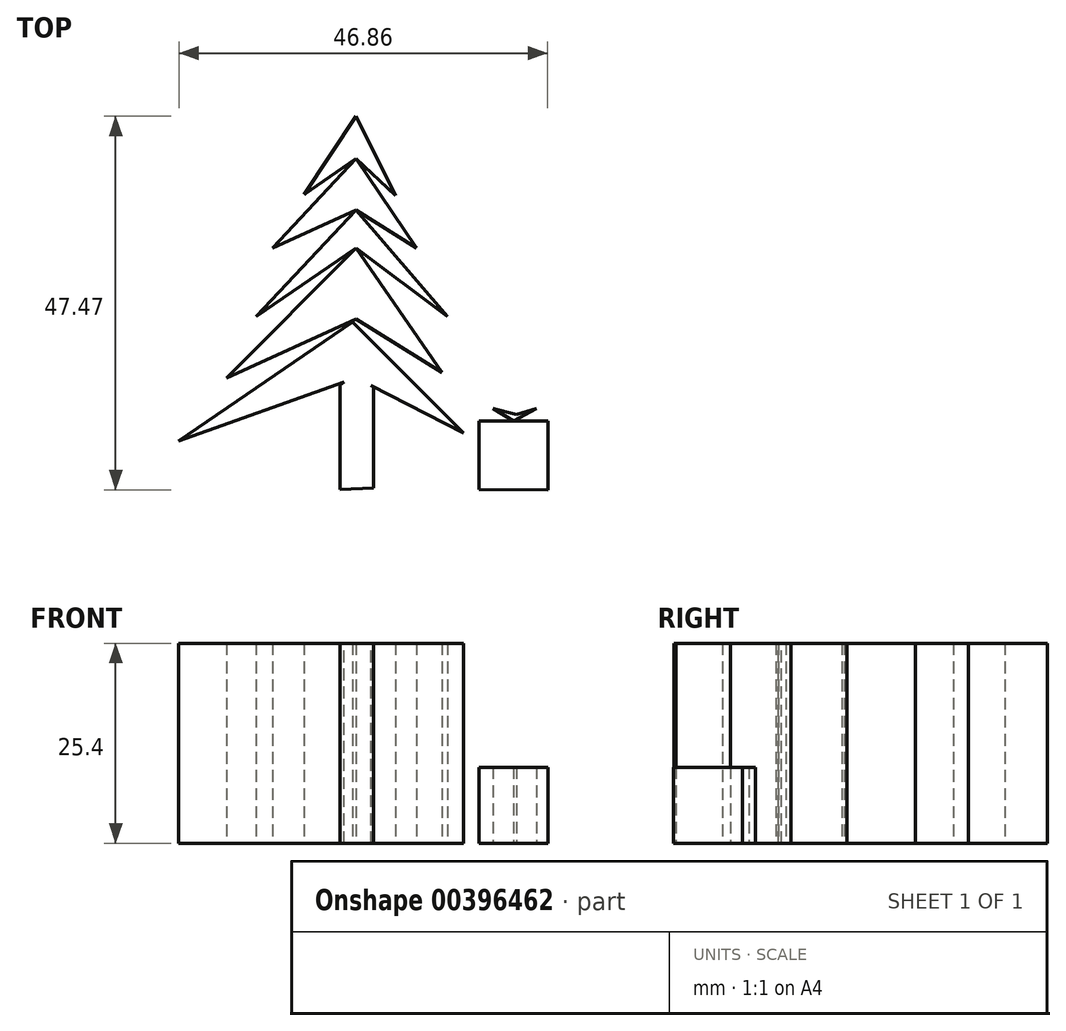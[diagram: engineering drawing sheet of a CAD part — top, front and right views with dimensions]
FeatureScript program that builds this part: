
annotation { "Feature Type Name" : "Feature", "Feature Type Description" : "" }
export const myFeature = defineFeature(function(context is Context, id is Id, definition is map)
    precondition{}
    {
        {
            var Q0;
            Q0=qCreatedBy(makeId("Top.planeOp"),FACE);
            var sketch = newSketch(context, id + "F0", { "sketchPlane" : qUnion([Q0])});
            skLineSegment(sketch, "E0", {"start": v(-12.69, -29.61) * mm, "end": v(0, -20.88) * mm});
            skLineSegment(sketch, "E1", {"start": v(0, -20.88) * mm, "end": v(11.61, -29.58) * mm});
            skLineSegment(sketch, "E2", {"start": v(-12.69, -29.61) * mm, "end": v(0, -16.07) * mm});
            skLineSegment(sketch, "E3", {"start": v(0, -16.07) * mm, "end": v(-10.65, -20.88) * mm});
            skLineSegment(sketch, "E4", {"start": v(-10.65, -20.88) * mm, "end": v(0, -9.51) * mm});
            skLineSegment(sketch, "E5", {"start": v(0, -9.51) * mm, "end": v(-6.63, -14.07) * mm});
            skLineSegment(sketch, "E6", {"start": v(-6.63, -14.07) * mm, "end": v(0, -4.13) * mm});
            skLineSegment(sketch, "E7", {"start": v(0, -16.07) * mm, "end": v(11.61, -29.58) * mm});
            skLineSegment(sketch, "E8", {"start": v(0, -16.07) * mm, "end": v(7.66, -20.88) * mm});
            skLineSegment(sketch, "E9", {"start": v(0, -9.51) * mm, "end": v(7.66, -20.88) * mm});
            skLineSegment(sketch, "E10", {"start": v(0, -9.51) * mm, "end": v(5, -14.2) * mm});
            skLineSegment(sketch, "E11", {"start": v(0, -4.13) * mm, "end": v(5, -14.2) * mm});
            skLineSegment(sketch, "E12", {"start": v(0, -20.88) * mm, "end": v(-16.49, -37.36) * mm});
            skLineSegment(sketch, "E13", {"start": v(0, -20.88) * mm, "end": v(10.9, -36.72) * mm});
            skLineSegment(sketch, "E14", {"start": v(-16.49, -37.36) * mm, "end": v(0, -29.91) * mm});
            skLineSegment(sketch, "E15", {"start": v(0, -29.91) * mm, "end": v(10.9, -36.72) * mm});
            skLineSegment(sketch, "E16", {"start": v(0, -29.91) * mm, "end": v(-22.53, -45.41) * mm});
            skLineSegment(sketch, "E17", {"start": v(-0.5, -30.24) * mm, "end": v(13.63, -44.38) * mm});
            skLineSegment(sketch, "E18", {"start": v(-22.53, -45.41) * mm, "end": v(0, -37.36) * mm});
            skLineSegment(sketch, "E19", {"start": v(0, -37.36) * mm, "end": v(13.63, -44.38) * mm});
            skLineSegment(sketch, "E20", {"start": v(0, 8.52) * mm, "end": v(-3.74, 0) * mm});
            skLineSegment(sketch, "E21", {"start": v(0, 8.52) * mm, "end": v(3.8, 0) * mm});
            skLineSegment(sketch, "E22", {"start": v(3.8, 0) * mm, "end": v(10.42, 2.95) * mm});
            skLineSegment(sketch, "E23", {"start": v(10.42, 2.95) * mm, "end": v(3.8, -2.33) * mm});
            skLineSegment(sketch, "E24", {"start": v(3.8, -2.33) * mm, "end": v(7.15, -6.53) * mm});
            skLineSegment(sketch, "E25", {"start": v(7.15, -6.53) * mm, "end": v(0, -4.13) * mm});
            skLineSegment(sketch, "E26", {"start": v(-3.74, 0) * mm, "end": v(-10.47, 2.95) * mm});
            skLineSegment(sketch, "E27", {"start": v(-10.47, 2.95) * mm, "end": v(-6.24, -2.33) * mm});
            skLineSegment(sketch, "E28", {"start": v(-6.24, -2.33) * mm, "end": v(-8.09, -6.53) * mm});
            skLineSegment(sketch, "E29", {"start": v(-7.4, -6.56) * mm, "end": v(0, -4.13) * mm});
            skSolve(sketch);
        }
        {
            var Q0;
            Q0 = qSketchRegion(id + "F0", true);
            extrude(context, id + "F1", {"entities" : qUnion([Q0]), "depth" : 25.4 * mm});
        }
        {
            var Q0;
            Q0=qCreatedBy(makeId("Top.planeOp"),FACE);
            var sketch = newSketch(context, id + "F2", { "sketchPlane" : qUnion([Q0])});
            skLineSegment(sketch, "E30", {"start": v(2.19, -38.6) * mm, "end": v(2.19, -51.33) * mm});
            skLineSegment(sketch, "E31", {"start": v(-2.06, -38.3) * mm, "end": v(-2.06, -51.55) * mm});
            skLineSegment(sketch, "E32", {"start": v(2.19, -51.33) * mm, "end": v(-2.06, -51.55) * mm});
            skLineSegment(sketch, "E33", {"start": v(2.19, -38.6) * mm, "end": v(0, -36.75) * mm});
            skLineSegment(sketch, "E34", {"start": v(-2.06, -38.3) * mm, "end": v(0, -36.75) * mm});
            skSolve(sketch);
        }
        {
            var Q0;
            Q0 = qSketchRegion(id + "F2", true);
            extrude(context, id + "F3", {"entities" : qUnion([Q0]), "operationType" : NewBodyOperationType.ADD, "depth" : 25.4 * mm});
        }
        {
            var Q0;
            Q0=qCreatedBy(makeId("Top.planeOp"),FACE);
            var sketch = newSketch(context, id + "F4", { "sketchPlane" : qUnion([Q0])});
            skLineSegment(sketch, "E35", {"start": v(15.6, -51.52) * mm, "end": v(15.6, -42.83) * mm});
            skLineSegment(sketch, "E36", {"start": v(15.6, -42.83) * mm, "end": v(24.33, -42.83) * mm});
            skLineSegment(sketch, "E37", {"start": v(24.33, -42.83) * mm, "end": v(24.33, -51.6) * mm});
            skLineSegment(sketch, "E38", {"start": v(15.6, -51.52) * mm, "end": v(24.33, -51.6) * mm});
            skLineSegment(sketch, "E39", {"start": v(17.35, -41.24) * mm, "end": v(19.97, -42.83) * mm});
            skLineSegment(sketch, "E40", {"start": v(17.35, -41.24) * mm, "end": v(20.4, -42.04) * mm});
            skPoint(sketch, "E40.endSnap0", {"position": v(18.66, -42.04) * mm});
            skLineSegment(sketch, "E41", {"start": v(20.4, -42.04) * mm, "end": v(22.93, -41.24) * mm});
            skLineSegment(sketch, "E42", {"start": v(22.93, -41.24) * mm, "end": v(19.97, -42.83) * mm});
            skSolve(sketch);
        }
        {
            var Q0;
            Q0 = qSketchRegion(id + "F4", true);
            extrude(context, id + "F5", {"entities" : qUnion([Q0]), "depth" : 9.65 * mm});
        }
    });
